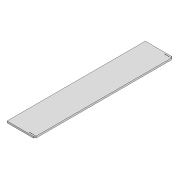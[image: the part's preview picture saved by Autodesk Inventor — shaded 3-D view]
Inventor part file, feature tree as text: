
AUTODESK INVENTOR PART (.ipt)
format: ipt  version: 2022 (Build 260153000, 153)  size: 114,176 bytes
history: native  units: mm
features: extrude x3, sketch x3, pattern_linear x1, plane x1, mirror x1
ambient origin geometry x8: Origin, YZ Plane, XZ Plane, XY Plane, X Axis, Y Axis, Z Axis, Center Point
bodies: Solid1 (feature_tree)
feature tree (9):
  extrude  "Extrusion1"  Depth=100.0mm
  extrude  "Extrusion2"  Depth=6.0mm
  pattern_linear  "Rectangular Pattern1"  Spacing1=10.0mm  [1 undecoded]
  plane  "Work Plane1"
  extrude  "Extrusion3"  Depth=10.0mm TaperAngle=0.0deg
  mirror  "Mirror1"
  sketch  "Sketch1"  dims[d0=500.0mm d1=100.0mm]
  sketch  "Sketch2"  dims[d2=6.0mm d3=0.0mm d4=2.95mm]
  sketch  "Sketch3"  dims[d5=5.0mm d6=10.0mm d7=10.0mm d8=0.0mm d9=30.0mm d11=6.0mm d12=4.0mm d13=5.0mm d14=100.0mm d15=0.0mm]
note: 1 required parameter value undecoded (feature->parameter linkage not recoverable at this tier; creation-order binding heuristic only, values carry confidence <= 0.55)
